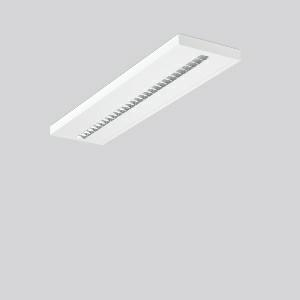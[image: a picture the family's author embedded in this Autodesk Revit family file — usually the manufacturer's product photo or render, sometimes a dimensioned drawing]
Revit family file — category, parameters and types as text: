
# Revit family: sonis_901690_002_1_70c0
name_source: partatom
category: Lighting Fixtures
units: mm (PartAtom-declared; Revit-internal decimal feet)

## family parameters
Cut with Voids When Loaded = No
Host = Face
Light Source = No
Part Type = Normal
Room Calculation Point = No
Round Connector Dimension = Use Diameter
Shared = No

## types (1)
- SONIS (1 x LED Modul 840, 3450 lm, 4000)
    Apparent Load = 26 VA
    CIE Flux Codes = 82 100 100 100 100
    Color Rendering = 80
    Color Temperature = 4000
    Default Elevation = 1800 mm
    Description = Series: SONIS
High-efficiency LED louvre surface-mounted luminaire. Housing: metal, powder-coated. Alea optical system: Reflector structure (ABS, Aluminium-coated, highly polished) with integrated diffuser made of non-yellowing plastic (PMMA) opal for glare-free light at the workstation. Narrow beam, brilliant luminous effect. Suitable for Ceiling mounting. Driver integrated. Perfect for office areas (RUG < 19) and environments with computer screens in accordance with EN 12464-1. 
Colour: white
Length: 1202 mm
Width: 302 mm
Height: 47 mm
Lamp: LED
Socket: without socket
Colour temperature: 4000K
Colour rendering index (CRI): 80
System power: 26 W
Rated luminous flux: 3450 lm
Luminous efficiency: 133 lm/W
Control gear: Regulated power supply
Protection class: I
Type of protection: IP 20
    Height = 33 mm
    Lamp = 1 x LED Modul 840
    Lamp Light Flux = 3450 lm
    Lamp count = 1
    Length = 1202 mm
    Lifetime = 50000 h
    Luminous efficacy = 133 lm/W
    Manufacturer = RZB
    ModVariant = No
    Model = 901690.002.1
    Mounting Place = Ceiling
    Mounting Type = Surface mounted
    Number of Poles = 1
    OnlyDefault = Yes
    Power Factor = 1
    Product Name = SONIS
    Product group = Surface mounted modular luminaires
    ProductGroupID = 306
    Protection Class = Protection class I
    Protection Degree = IP 20
    RLX_Detail_Level = 1
    RLX_Emergency_Light_Flux = 0 lm
    RLX_Emergency_Type = 0
    RLX_Emergency_Type_DB = No
    RlxData = <blob elided: 23821 chars, md5=36c455b8>
    Socket = socket
    Standby Power = 0 W
    System Light Flux = 3450 lm
    System Power = 26 W
    Type Comments = Product without accessories
    Type Image = 901627.002.jpg
    URL = http://relux.com
    VarID = ---
    Voltage = 230 V
    Voltage Range = 220-240 V
    Weight = 0.00 kg
    Width = 302 mm

## geometry (parser evidence)
native form markers: Blend x4, Sweep x10
no freeform markers — native parametric forms only
